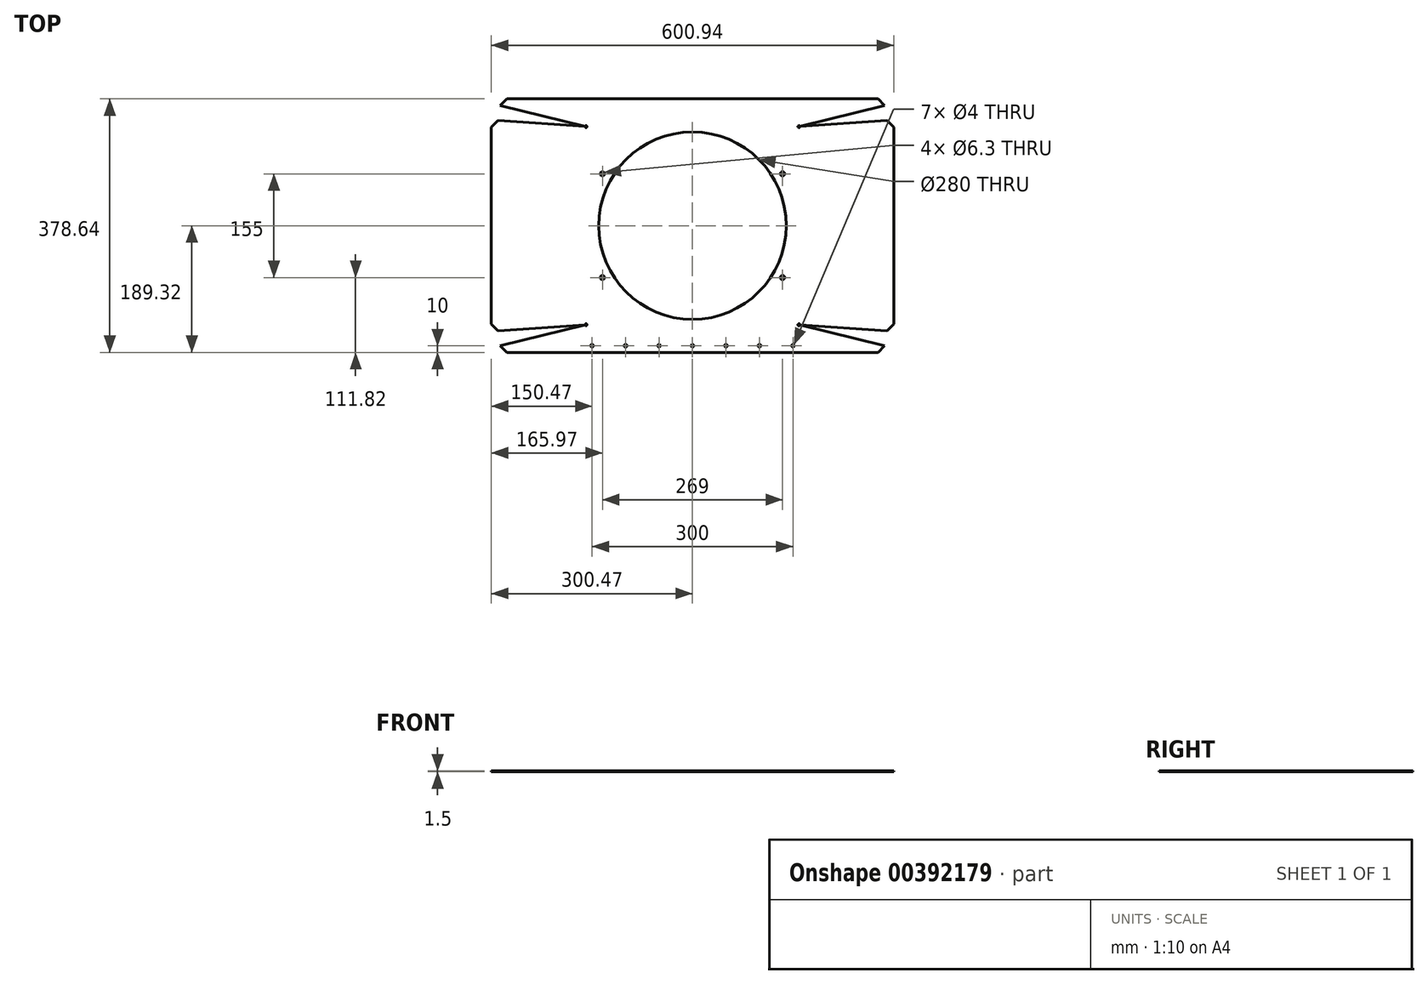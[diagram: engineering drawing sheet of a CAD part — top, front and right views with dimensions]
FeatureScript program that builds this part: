
annotation { "Feature Type Name" : "Feature", "Feature Type Description" : "" }
export const myFeature = defineFeature(function(context is Context, id is Id, definition is map)
    precondition{}
    {
        {
            var Q0;
            Q0=qCreatedBy(makeId("Top.planeOp"),FACE);
            var sketch = newSketch(context, id + "F0", { "sketchPlane" : qUnion([Q0])});
            skLineSegment(sketch, "E0.bottom", {"start": v(159, 148) * mm, "end": v(-159, 148) * mm, "construction": true});
            skLineSegment(sketch, "E0.top", {"start": v(159, -148) * mm, "end": v(-159, -148) * mm, "construction": true});
            skLineSegment(sketch, "E0.left", {"start": v(159, 148) * mm, "end": v(159, -148) * mm, "construction": true});
            skLineSegment(sketch, "E0.right", {"start": v(-159, 148) * mm, "end": v(-159, -148) * mm, "construction": true});
            skPoint(sketch, "E0.middle", {"position": v(0, 0) * mm});
            skCircle(sketch, "E1", {"center": v(0, 0) * mm, "radius": 140 * mm});
            skLineSegment(sketch, "E2.bottom", {"start": v(-134.5, 77.5) * mm, "end": v(134.5, 77.5) * mm, "construction": true});
            skLineSegment(sketch, "E2.top", {"start": v(-134.5, -77.5) * mm, "end": v(134.5, -77.5) * mm, "construction": true});
            skLineSegment(sketch, "E2.left", {"start": v(-134.5, 77.5) * mm, "end": v(-134.5, -77.5) * mm, "construction": true});
            skLineSegment(sketch, "E2.right", {"start": v(134.5, 77.5) * mm, "end": v(134.5, -77.5) * mm, "construction": true});
            skCircle(sketch, "E3", {"center": v(-134.5, 77.5) * mm, "radius": 3.15 * mm});
            skCircle(sketch, "E4", {"center": v(134.5, 77.5) * mm, "radius": 3.15 * mm});
            skCircle(sketch, "E5", {"center": v(-134.5, -77.5) * mm, "radius": 3.15 * mm});
            skCircle(sketch, "E6", {"center": v(134.5, -77.5) * mm, "radius": 3.15 * mm});
            skLineSegment(sketch, "E7", {"start": v(-287, -179.32) * mm, "end": v(287, -179.32) * mm, "construction": true});
            skPoint(sketch, "E8", {"position": v(0, -179.32) * mm});
            skLineSegment(sketch, "E9", {"start": v(0, -179.32) * mm, "end": v(0, 179.32) * mm, "construction": true});
            skPoint(sketch, "E9.startSnap0", {"position": v(0, -148) * mm});
            skPoint(sketch, "E9.endSnap0", {"position": v(0, 77.5) * mm});
            skLineSegment(sketch, "E10", {"start": v(-287, -179.32) * mm, "end": v(-160.46, -148.36) * mm});
            skLineSegment(sketch, "E11", {"start": v(160.46, -148.36) * mm, "end": v(287, -179.32) * mm});
            skLineSegment(sketch, "E12", {"start": v(-290.47, 0) * mm, "end": v(290.47, 0) * mm, "construction": true});
            skLineSegment(sketch, "E13", {"start": v(290.47, 157) * mm, "end": v(290.47, -157) * mm, "construction": true});
            skPoint(sketch, "E14", {"position": v(290.47, 0) * mm});
            skLineSegment(sketch, "E15", {"start": v(160.5, 148.1) * mm, "end": v(290.47, 157) * mm});
            skLineSegment(sketch, "E16", {"start": v(160.5, -148.1) * mm, "end": v(290.47, -157) * mm});
            skLineSegment(sketch, "E17", {"start": v(-290.47, 157) * mm, "end": v(-290.47, -157) * mm, "construction": true});
            skPoint(sketch, "E18", {"position": v(-290.47, 0) * mm});
            skLineSegment(sketch, "E19", {"start": v(-290.47, -157) * mm, "end": v(-160.5, -148.1) * mm});
            skLineSegment(sketch, "E20", {"start": v(-290.47, 157) * mm, "end": v(-160.5, 148.1) * mm});
            skLineSegment(sketch, "E21", {"start": v(-287, 179.32) * mm, "end": v(287, 179.32) * mm, "construction": true});
            skPoint(sketch, "E22", {"position": v(0, 179.32) * mm});
            skLineSegment(sketch, "E23", {"start": v(-287, 179.32) * mm, "end": v(-160.46, 148.36) * mm});
            skLineSegment(sketch, "E24", {"start": v(160.46, 148.36) * mm, "end": v(287, 179.32) * mm});
            skArc(sketch, "E25", {"start": v(-160.5, 148.1) * mm, "mid": v(-157.52, 147.77) * mm, "end": v(-160.46, 148.36) * mm});
            skArc(sketch, "E26", {"start": v(160.46, 148.36) * mm, "mid": v(157.52, 147.77) * mm, "end": v(160.5, 148.1) * mm});
            skArc(sketch, "E27", {"start": v(-160.46, -148.36) * mm, "mid": v(-157.52, -147.77) * mm, "end": v(-160.5, -148.1) * mm});
            skArc(sketch, "E28", {"start": v(160.5, -148.1) * mm, "mid": v(157.52, -147.77) * mm, "end": v(160.46, -148.36) * mm});
            skLineSegment(sketch, "E29", {"start": v(-290.47, 157) * mm, "end": v(-300.47, 147) * mm});
            skLineSegment(sketch, "E30", {"start": v(-300.47, 147) * mm, "end": v(-300.47, -147) * mm});
            skLineSegment(sketch, "E31", {"start": v(-300.47, -147) * mm, "end": v(-290.47, -157) * mm});
            skLineSegment(sketch, "E32", {"start": v(-277, 189.32) * mm, "end": v(-287, 179.32) * mm});
            skLineSegment(sketch, "E33", {"start": v(-277, 189.32) * mm, "end": v(277, 189.32) * mm});
            skLineSegment(sketch, "E34", {"start": v(277, 189.32) * mm, "end": v(287, 179.32) * mm});
            skLineSegment(sketch, "E35", {"start": v(290.47, 157) * mm, "end": v(300.47, 147) * mm});
            skLineSegment(sketch, "E36", {"start": v(300.47, 147) * mm, "end": v(300.47, -147) * mm});
            skLineSegment(sketch, "E37", {"start": v(300.47, -147) * mm, "end": v(290.47, -157) * mm});
            skLineSegment(sketch, "E38", {"start": v(-287, -179.32) * mm, "end": v(-277, -189.32) * mm});
            skLineSegment(sketch, "E39", {"start": v(-277, -189.32) * mm, "end": v(277, -189.32) * mm});
            skLineSegment(sketch, "E40", {"start": v(277, -189.32) * mm, "end": v(287, -179.32) * mm});
            skCircle(sketch, "E41", {"center": v(0, -179.32) * mm, "radius": 2 * mm});
            skPoint(sketch, "E42", {"position": v(50, -179.32) * mm});
            skPoint(sketch, "E43", {"position": v(100, -179.32) * mm});
            skPoint(sketch, "E44", {"position": v(150, -179.32) * mm});
            skPoint(sketch, "E45", {"position": v(-50, -179.32) * mm});
            skPoint(sketch, "E46", {"position": v(-100, -179.32) * mm});
            skPoint(sketch, "E47", {"position": v(-150, -179.32) * mm});
            skCircle(sketch, "E48", {"center": v(-150, -179.32) * mm, "radius": 2 * mm});
            skCircle(sketch, "E49", {"center": v(-100, -179.32) * mm, "radius": 2 * mm});
            skCircle(sketch, "E50", {"center": v(-50, -179.32) * mm, "radius": 2 * mm});
            skCircle(sketch, "E51", {"center": v(50, -179.32) * mm, "radius": 2 * mm});
            skCircle(sketch, "E52", {"center": v(100, -179.32) * mm, "radius": 2 * mm});
            skCircle(sketch, "E53", {"center": v(150, -179.32) * mm, "radius": 2 * mm});
            skSolve(sketch);
        }
        {
            var Q0;
            Q0 = qSketchRegion(id + "F0", true);
            extrude(context, id + "F1", {"entities" : qUnion([Q0]), "depth" : 1.5 * mm});
        }
    });
